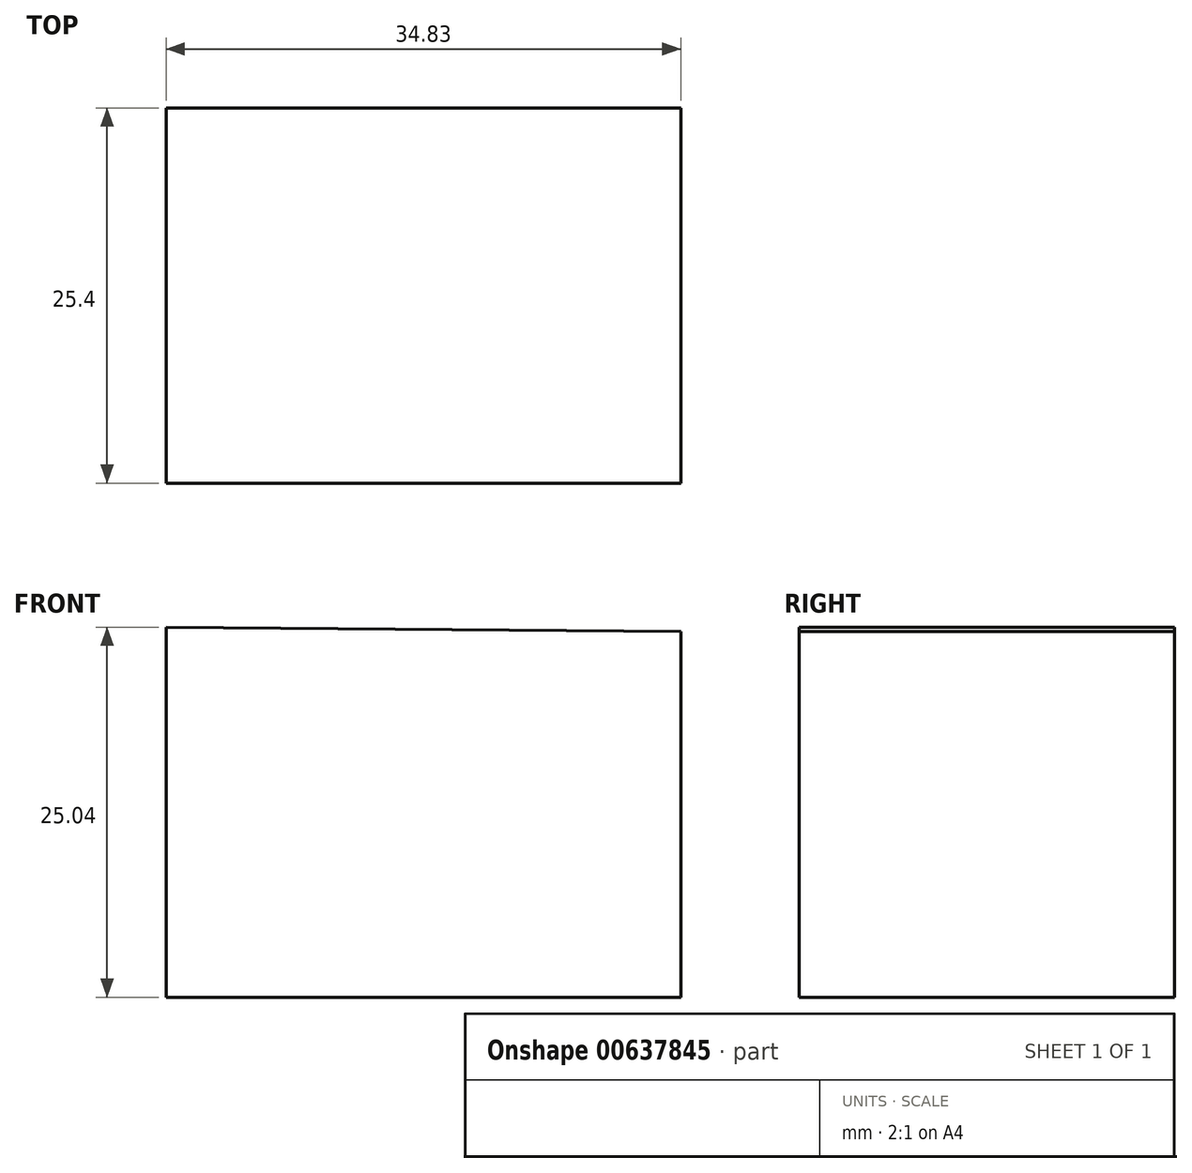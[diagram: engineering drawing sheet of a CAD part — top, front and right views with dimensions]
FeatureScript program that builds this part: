
annotation { "Feature Type Name" : "Feature", "Feature Type Description" : "" }
export const myFeature = defineFeature(function(context is Context, id is Id, definition is map)
    precondition{}
    {
        {
            var Q0;
            Q0=qCreatedBy(makeId("Front.planeOp"),FACE);
            var sketch = newSketch(context, id + "F0", { "sketchPlane" : qUnion([Q0])});
            skLineSegment(sketch, "E0", {"start": v(-55.98, 46.48) * mm, "end": v(-55.98, 21.44) * mm});
            skLineSegment(sketch, "E1", {"start": v(-55.98, 21.44) * mm, "end": v(-21.15, 21.44) * mm});
            skLineSegment(sketch, "E2", {"start": v(-21.15, 21.44) * mm, "end": v(-21.15, 46.2) * mm});
            skLineSegment(sketch, "E3", {"start": v(-21.15, 46.2) * mm, "end": v(-55.98, 46.48) * mm});
            skSolve(sketch);
        }
        {
            var Q0;
            Q0 = qSketchRegion(id + "F0", true);
            extrude(context, id + "F1", {"entities" : qUnion([Q0]), "depth" : 25.4 * mm, "offsetDistance" : 25.4 * mm});
        }
    });
